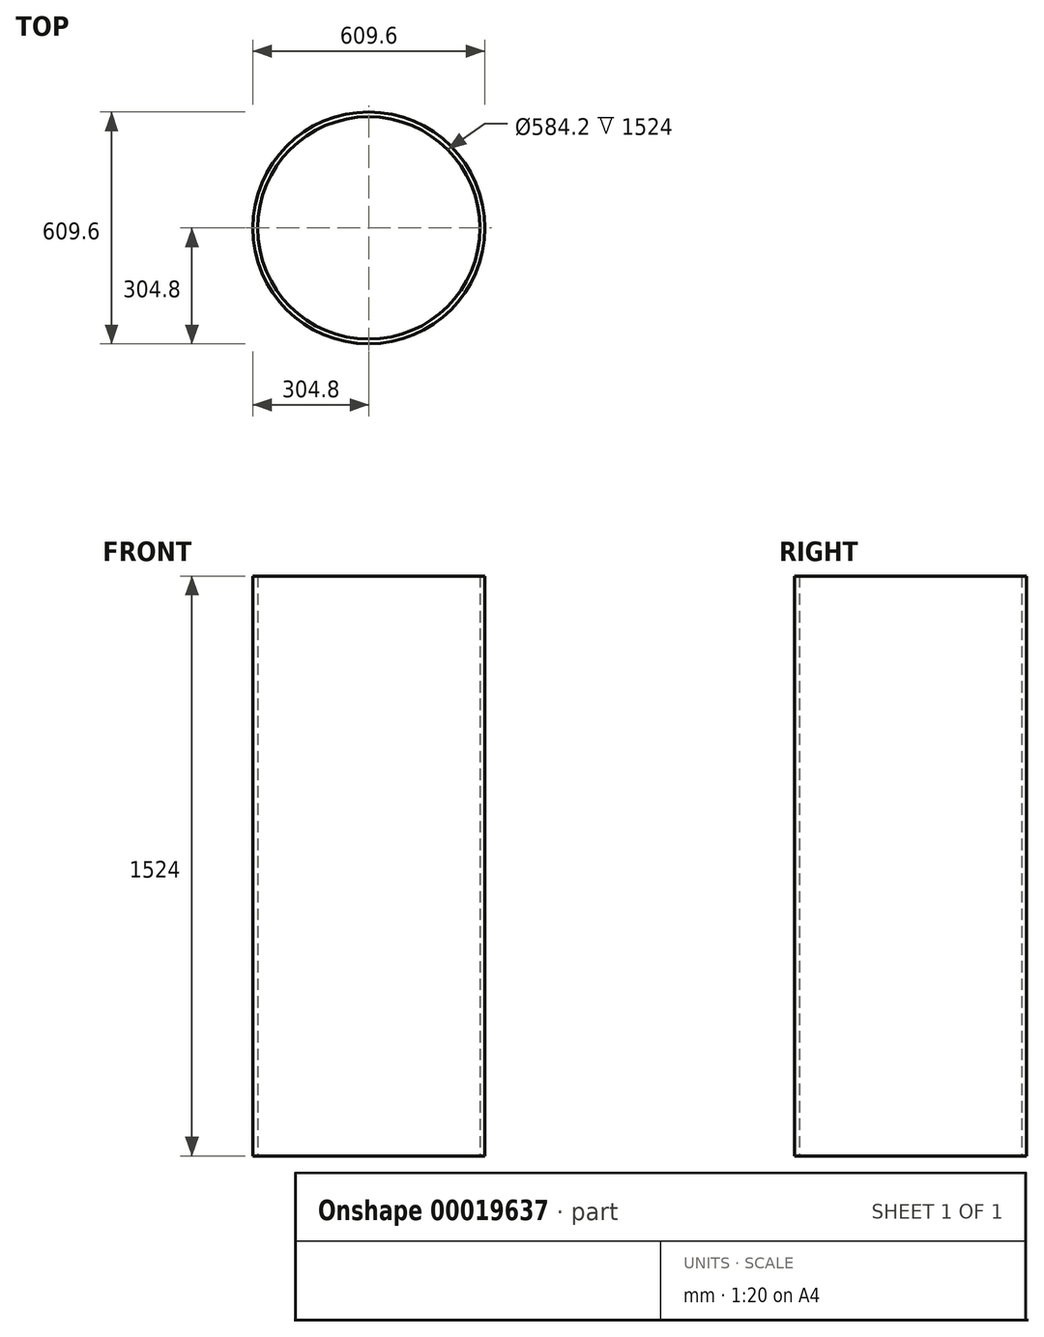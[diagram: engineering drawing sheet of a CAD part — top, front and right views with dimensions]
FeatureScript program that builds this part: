
annotation { "Feature Type Name" : "Feature", "Feature Type Description" : "" }
export const myFeature = defineFeature(function(context is Context, id is Id, definition is map)
    precondition{}
    {
        {
            var Q0;
            Q0=qCreatedBy(makeId("Top.planeOp"),FACE);
            var sketch = newSketch(context, id + "F0", { "sketchPlane" : qUnion([Q0])});
            skCircle(sketch, "E0", {"center": v(0, 0) * mm, "radius": 304.8 * mm});
            skCircle(sketch, "E1", {"center": v(0, 0) * mm, "radius": 292.1 * mm});
            skSolve(sketch);
        }
        {
            var Q0;
            Q0=makeQuery(id+"F0.imprint","IMPRINT",FACE,{"disambiguationData":[TD([[makeQuery(id+"F0.imprint","IMPRINT",EDGE,{"derivedFrom":sQuery(id+"F0.wireOp",EDGE,"E0")}),1.0]])]});
            extrude(context, id + "F1", {"entities" : qUnion([Q0]), "depth" : 1524 * mm});
        }
    });
